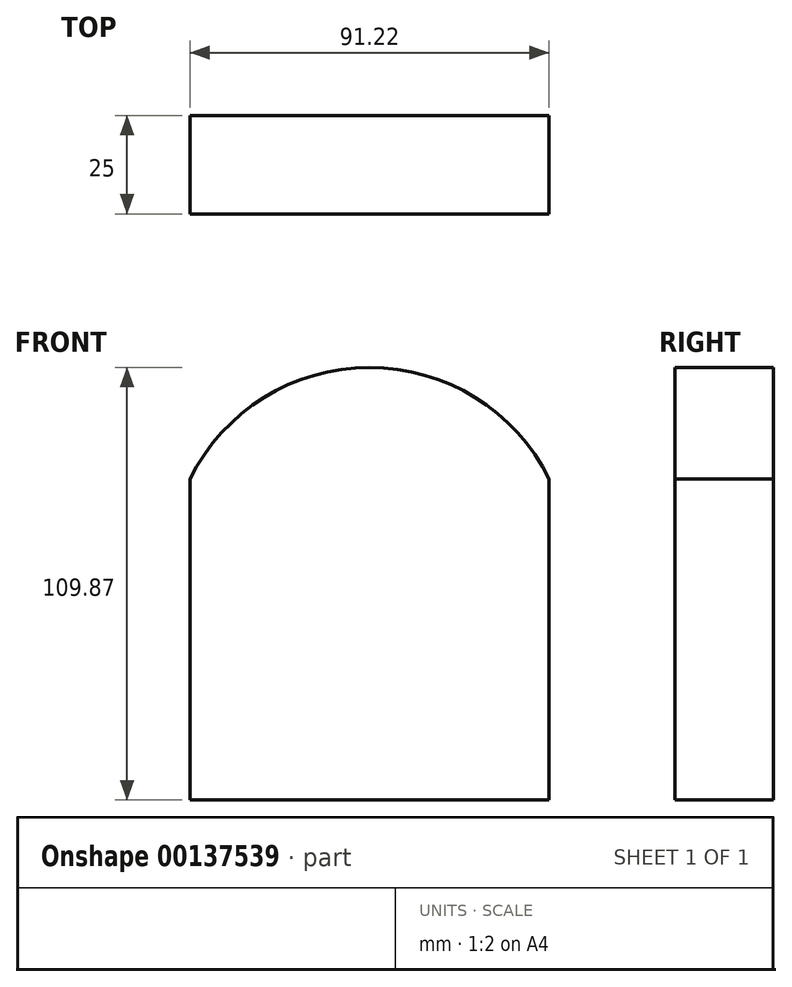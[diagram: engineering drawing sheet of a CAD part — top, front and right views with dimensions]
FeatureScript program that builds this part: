
annotation { "Feature Type Name" : "Feature", "Feature Type Description" : "" }
export const myFeature = defineFeature(function(context is Context, id is Id, definition is map)
    precondition{}
    {
        {
            var Q0;
            Q0=qCreatedBy(makeId("Front.planeOp"),FACE);
            var sketch = newSketch(context, id + "F0", { "sketchPlane" : qUnion([Q0])});
            skLineSegment(sketch, "E0.top", {"start": v(-111.08, -40.12) * mm, "end": v(-19.86, -40.12) * mm});
            skLineSegment(sketch, "E0.left", {"start": v(-111.08, 41.46) * mm, "end": v(-111.08, -40.12) * mm});
            skLineSegment(sketch, "E0.right", {"start": v(-19.86, 41.46) * mm, "end": v(-19.86, -40.12) * mm});
            skArc(sketch, "E1", {"start": v(-19.86, 41.46) * mm, "mid": v(-65.47, 69.75) * mm, "end": v(-111.08, 41.46) * mm});
            skSolve(sketch);
        }
        {
            var Q0;
            Q0=makeQuery(id+"F0.imprint","IMPRINT",FACE,{"disambiguationData":[TD([[makeQuery(id+"F0.imprint","IMPRINT",EDGE,{"derivedFrom":sQuery(id+"F0.wireOp",EDGE,"E0.top")}),1.0]])]});
            extrude(context, id + "F1", {"entities" : qUnion([Q0]), "depth" : 25 * mm});
        }
    });
